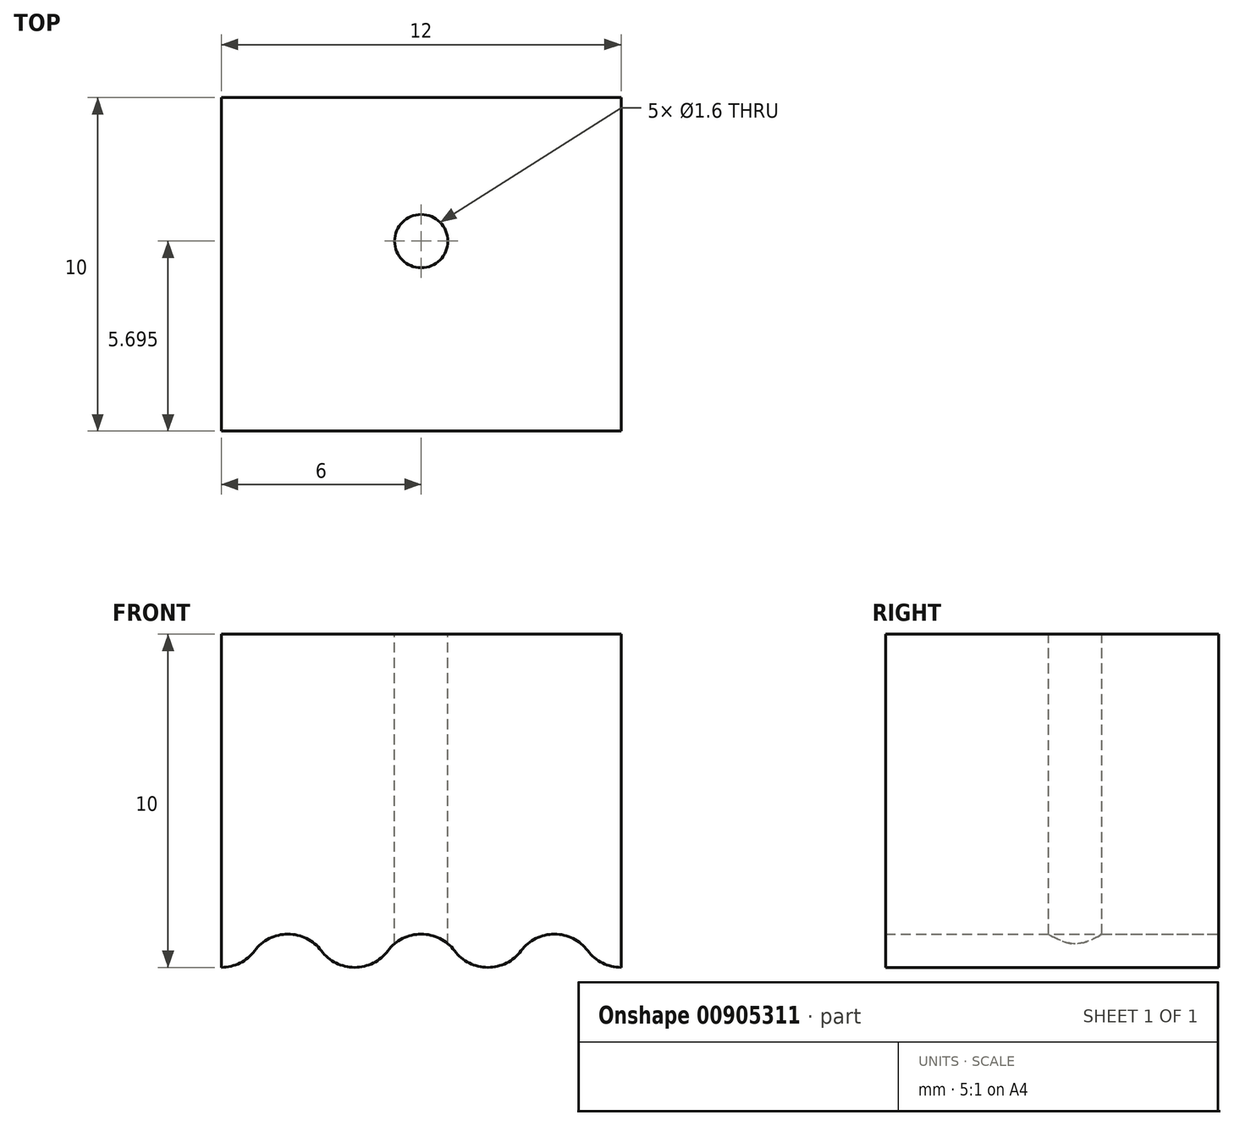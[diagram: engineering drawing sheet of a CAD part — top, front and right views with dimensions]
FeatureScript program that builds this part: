
annotation { "Feature Type Name" : "Feature", "Feature Type Description" : "" }
export const myFeature = defineFeature(function(context is Context, id is Id, definition is map)
    precondition{}
    {
        {
            var Q0;
            Q0=qCreatedBy(makeId("Front.planeOp"),FACE);
            var sketch = newSketch(context, id + "F0", { "sketchPlane" : qUnion([Q0])});
            skArc(sketch, "E0", {"start": v(-3, -4.5) * mm, "mid": v(-4, -4) * mm, "end": v(-5, -4.5) * mm});
            skArc(sketch, "E1", {"start": v(-6, -5) * mm, "mid": v(-5.44, -4.87) * mm, "end": v(-5, -4.5) * mm});
            skArc(sketch, "E2", {"start": v(5, -4.5) * mm, "mid": v(5.44, -4.87) * mm, "end": v(6, -5) * mm});
            skArc(sketch, "E3", {"start": v(5, -4.5) * mm, "mid": v(4, -4) * mm, "end": v(3, -4.5) * mm});
            skArc(sketch, "E4", {"start": v(1, -4.5) * mm, "mid": v(2, -5) * mm, "end": v(3, -4.5) * mm});
            skArc(sketch, "E5", {"start": v(1, -4.5) * mm, "mid": v(0, -4) * mm, "end": v(-1, -4.5) * mm});
            skArc(sketch, "E6", {"start": v(-3, -4.5) * mm, "mid": v(-2, -5) * mm, "end": v(-1, -4.5) * mm});
            skLineSegment(sketch, "E7", {"start": v(-6, -5) * mm, "end": v(-6, 5) * mm});
            skLineSegment(sketch, "E8", {"start": v(6, -5) * mm, "end": v(6, 5) * mm});
            skLineSegment(sketch, "E9", {"start": v(6, 5) * mm, "end": v(-6, 5) * mm});
            skSolve(sketch);
        }
        {
            var Q0;
            Q0=makeQuery(id+"F0.imprint","IMPRINT",FACE,{"disambiguationData":[TD([[makeQuery(id+"F0.imprint","IMPRINT",EDGE,{"derivedFrom":sQuery(id+"F0.wireOp",EDGE,"E0")}),-1.0]])]});
            extrude(context, id + "F1", {"entities" : qUnion([Q0]), "depth" : 10 * mm, "offsetDistance" : 25 * mm});
        }
        {
            var Q0;
            Q0=makeQuery(id+"F1.opExtrude","SWEPT_FACE",FACE,{"disambiguationData":[OSD([sQuery(id+"F0.wireOp",EDGE,"E9")])]});
            var sketch = newSketch(context, id + "F2", { "sketchPlane" : qUnion([Q0])});
            skLineSegment(sketch, "E10", {"start": v(-6, -4.05) * mm, "end": v(6, -4.56) * mm, "construction": true});
            skLineSegment(sketch, "E11", {"start": v(0, -10) * mm, "end": v(0, 0) * mm, "construction": true});
            skCircle(sketch, "E12", {"center": v(0, -4.3) * mm, "radius": 0.8 * mm});
            skSolve(sketch);
        }
        {
            var Q0;
            Q0=makeQuery(id+"F2.imprint","IMPRINT",FACE,{"disambiguationData":[TD([[makeQuery(id+"F2.imprint","IMPRINT",EDGE,{"derivedFrom":sQuery(id+"F2.wireOp",EDGE,"E12")}),1.0]])]});
            extrude(context, id + "F3", {"entities" : qUnion([Q0]), "operationType" : NewBodyOperationType.REMOVE, "oppositeDirection" : true, "depth" : 25 * mm, "offsetDistance" : 25 * mm});
        }
    });
